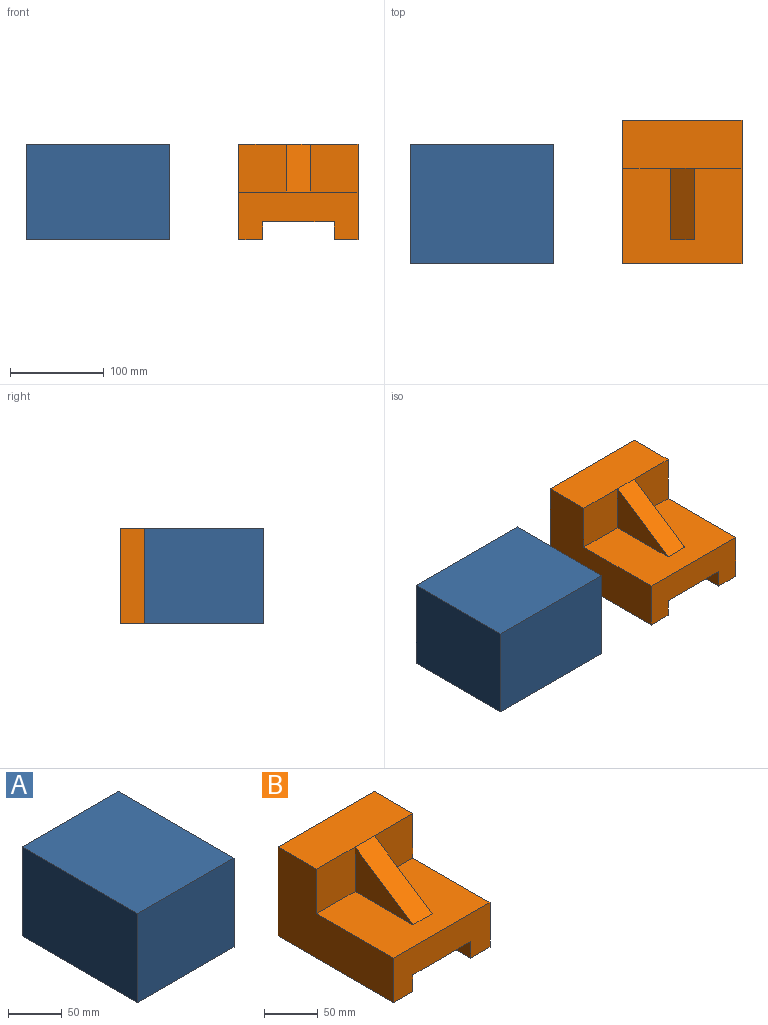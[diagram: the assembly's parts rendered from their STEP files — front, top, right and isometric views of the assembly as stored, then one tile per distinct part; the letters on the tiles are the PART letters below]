
ASSEMBLY  parts=2 mates=2
PART A: 6 faces, bbox 127x152.4x101.6 mm
  f0: plane 152.4x127mm, normal (0,0,-1), area 19354.8mm2, adj f1,f3,f4,f5
  f1: plane 152.4x101.6mm, normal (1,0,0), area 15483.8mm2, adj f0,f2,f4,f5
  f2: plane 152.4x127mm, normal (0,0,1), area 19354.8mm2, adj f1,f3,f4,f5
  f3: plane 152.4x101.6mm, normal (-1,0,0), area 15483.8mm2, adj f0,f2,f4,f5
  f4: plane 127x101.6mm, normal (0,-1,0), area 12903.2mm2, adj f0,f1,f2,f3
  f5: plane 127x101.6mm, normal (0,1,0), area 12903.2mm2, adj f0,f1,f2,f3
PART B: 16 faces, bbox 127x152.4x101.6 mm
  f0: plane 127x101.6mm, normal (0,0,1), area 10967.7mm2, adj f1,f2,f9,f10,f12,f13,f14,f15
  f1: plane 50.8x50.8mm, normal (0,-1,0), area 2580.6mm2, adj f0,f2,f3,f15
  f2: plane 152.4x101.6mm, normal (-1,0,0), area 10322.6mm2, adj f0,f1,f3,f4,f10,f11
  f3: plane 127x50.8mm, normal (0,0,1), area 6451.6mm2, adj f1,f2,f9,f11,f12,f13
  f4: plane 152.4x25.4mm, normal (0,0,-1), area 3871mm2, adj f2,f5,f10,f11
  f5: plane 152.4x19.13mm, normal (1,0,0), area 2915.8mm2, adj f4,f6,f10,f11
  f6: plane 152.4x76.2mm, normal (0,0,-1), area 11612.9mm2, adj f5,f7,f10,f11
  f7: plane 152.4x19.13mm, normal (-1,0,0), area 2915.8mm2, adj f6,f8,f10,f11
  f8: plane 152.4x25.4mm, normal (0,0,-1), area 3871mm2, adj f7,f9,f10,f11
  f9: plane 152.4x101.6mm, normal (1,0,0), area 10322.6mm2, adj f0,f3,f8,f10,f11,f12
  f10: plane 127x50.8mm, normal (0,-1,0), area 4993.7mm2, adj f0,f2,f4,f5,f6,f7,f8,f9
  f11: plane 127x101.6mm, normal (0,1,0), area 11445.3mm2, adj f2,f3,f4,f5,f6,f7,f8,f9
  f12: plane 50.8x50.8mm, normal (0,-1,0), area 2580.6mm2, adj f0,f3,f9,f14
  f13: plane 76.2x50.8mm, normal (0,-0.55,0.83), area 2326.2mm2, adj f0,f3,f14,f15
  f14: plane 76.2x50.8mm, normal (1,0,0), area 1935.5mm2, adj f0,f12,f13
  f15: plane 76.2x50.8mm, normal (-1,0,0), area 1935.5mm2, adj f0,f1,f13
PLACE A rot(axis=(0,0,1),90deg) t=(-305.02,225.81,-3.86)mm
PLACE B t=(-14.91,251.21,-3.86)mm
MATE planar A.f3 <-> B.f10  axis (0,-1,0) through (-229.08,98.81,46.94)mm
MATE planar A.f2 <-> B.f3  axis (0,0,1) through (-228.82,98.81,97.74)mm
